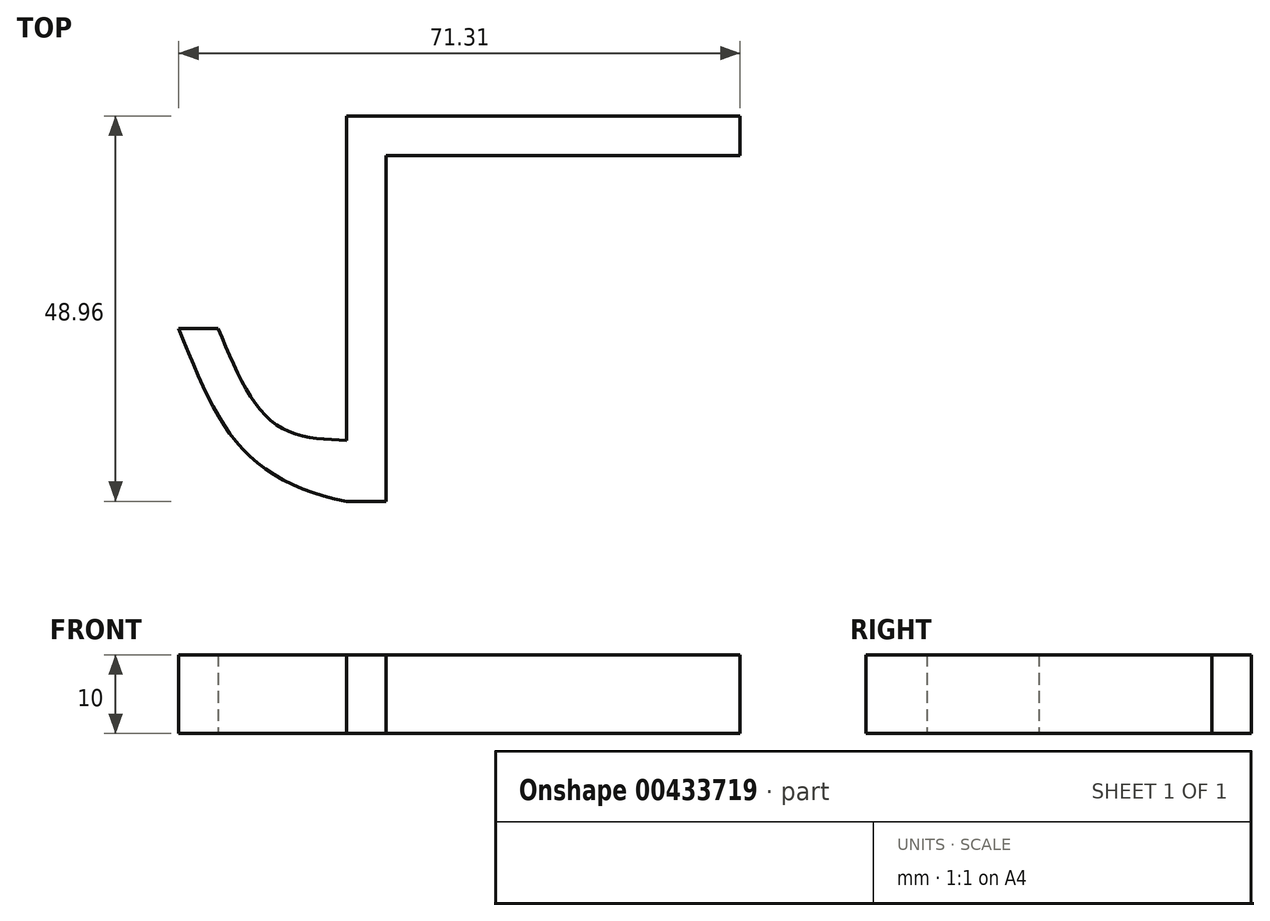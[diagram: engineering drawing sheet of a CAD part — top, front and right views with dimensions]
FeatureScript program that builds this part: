
annotation { "Feature Type Name" : "Feature", "Feature Type Description" : "" }
export const myFeature = defineFeature(function(context is Context, id is Id, definition is map)
    precondition{}
    {
        {
            var Q0;
            Q0=qCreatedBy(makeId("Top.planeOp"),FACE);
            var sketch = newSketch(context, id + "F0", { "sketchPlane" : qUnion([Q0])});
            skLineSegment(sketch, "E0.bottom", {"start": v(2.5, -21.98) * mm, "end": v(-2.5, -21.98) * mm});
            skLineSegment(sketch, "E0.left", {"start": v(2.5, -21.98) * mm, "end": v(2.5, 21.98) * mm});
            skLineSegment(sketch, "E0.right", {"start": v(-2.5, -14.22) * mm, "end": v(-2.5, 21.98) * mm});
            skPoint(sketch, "E0.middle", {"position": v(0, 0) * mm});
            skLineSegment(sketch, "E1.bottom", {"start": v(2.5, 21.98) * mm, "end": v(47.5, 21.98) * mm});
            skLineSegment(sketch, "E1.top", {"start": v(-2.5, 26.98) * mm, "end": v(47.5, 26.98) * mm});
            skLineSegment(sketch, "E1.left", {"start": v(-2.5, 21.98) * mm, "end": v(-2.5, 26.98) * mm});
            skLineSegment(sketch, "E1.right", {"start": v(47.5, 21.98) * mm, "end": v(47.5, 26.98) * mm});
            skFitSpline(sketch, "E2", {"points": [v(-2.5, -21.98) * mm, v(-15.74, -15.29) * mm, v(-23.8, 0) * mm], "startDerivative": vector(-34.82, 6.41) * mm, "endDerivative": vector(-14.94, 37.09) * mm});
            skLineSegment(sketch, "E3", {"start": v(-23.8, 0) * mm, "end": v(-18.8, 0) * mm});
            skFitSpline(sketch, "E4", {"points": [v(-18.8, 0) * mm, v(-11.63, -12.1) * mm, v(-2.5, -14.22) * mm], "startDerivative": vector(11.04, -26.7) * mm, "endDerivative": vector(21.95, -0.87) * mm});
            skSolve(sketch);
        }
        {
            var Q0;
            Q0 = qSketchRegion(id + "F0", true);
            extrude(context, id + "F1", {"entities" : qUnion([Q0]), "depth" : 10 * mm, "offsetDistance" : 25.4 * mm});
        }
    });
